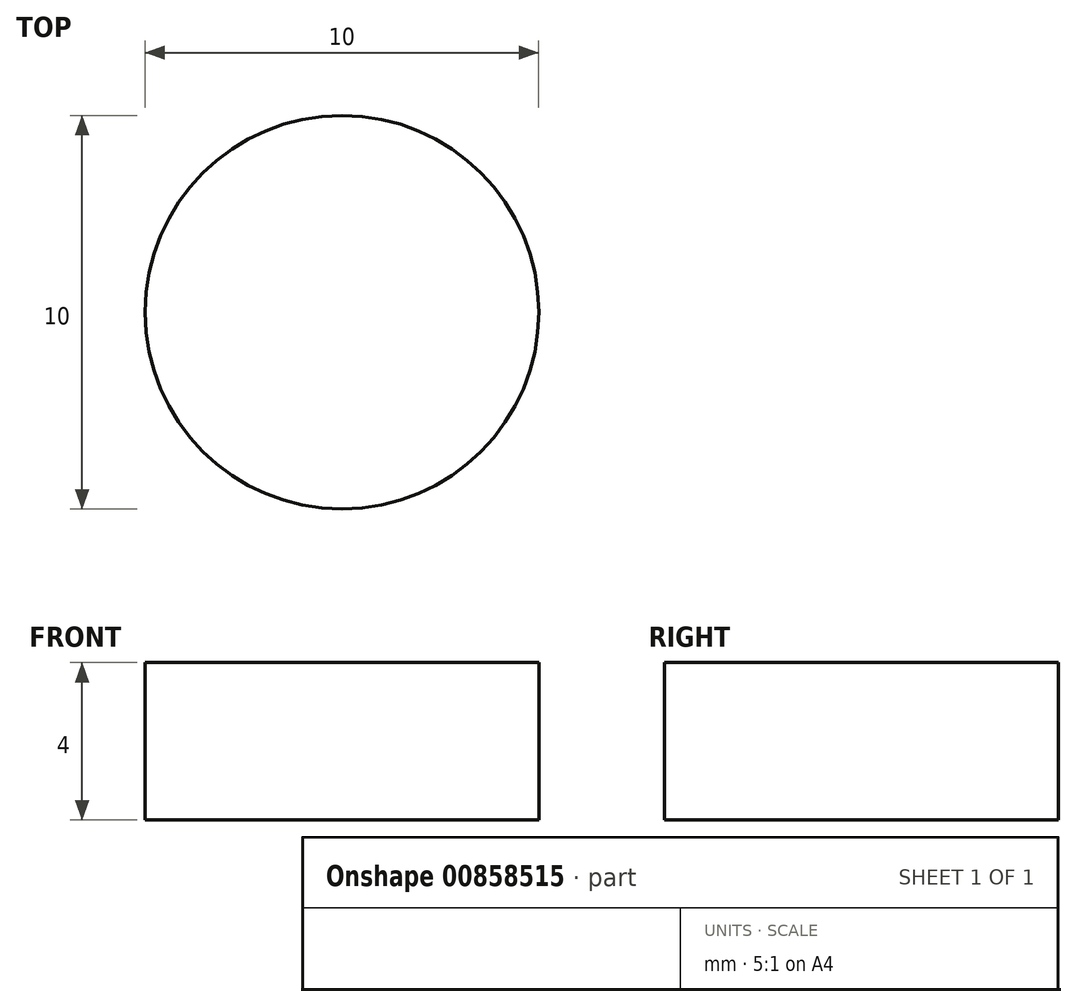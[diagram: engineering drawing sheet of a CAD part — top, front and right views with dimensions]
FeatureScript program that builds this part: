
annotation { "Feature Type Name" : "Feature", "Feature Type Description" : "" }
export const myFeature = defineFeature(function(context is Context, id is Id, definition is map)
    precondition{}
    {
        {
            var Q0;
            Q0=qCreatedBy(makeId("Top.planeOp"),FACE);
            var sketch = newSketch(context, id + "F0", { "sketchPlane" : qUnion([Q0])});
            skCircle(sketch, "E0", {"center": v(14.4, -9.29) * mm, "radius": 5 * mm});
            skSolve(sketch);
        }
        {
            var Q0;
            Q0 = qSketchRegion(id + "F0", true);
            extrude(context, id + "F1", {"entities" : qUnion([Q0]), "depth" : 4 * mm, "offsetDistance" : 25 * mm});
        }
    });
